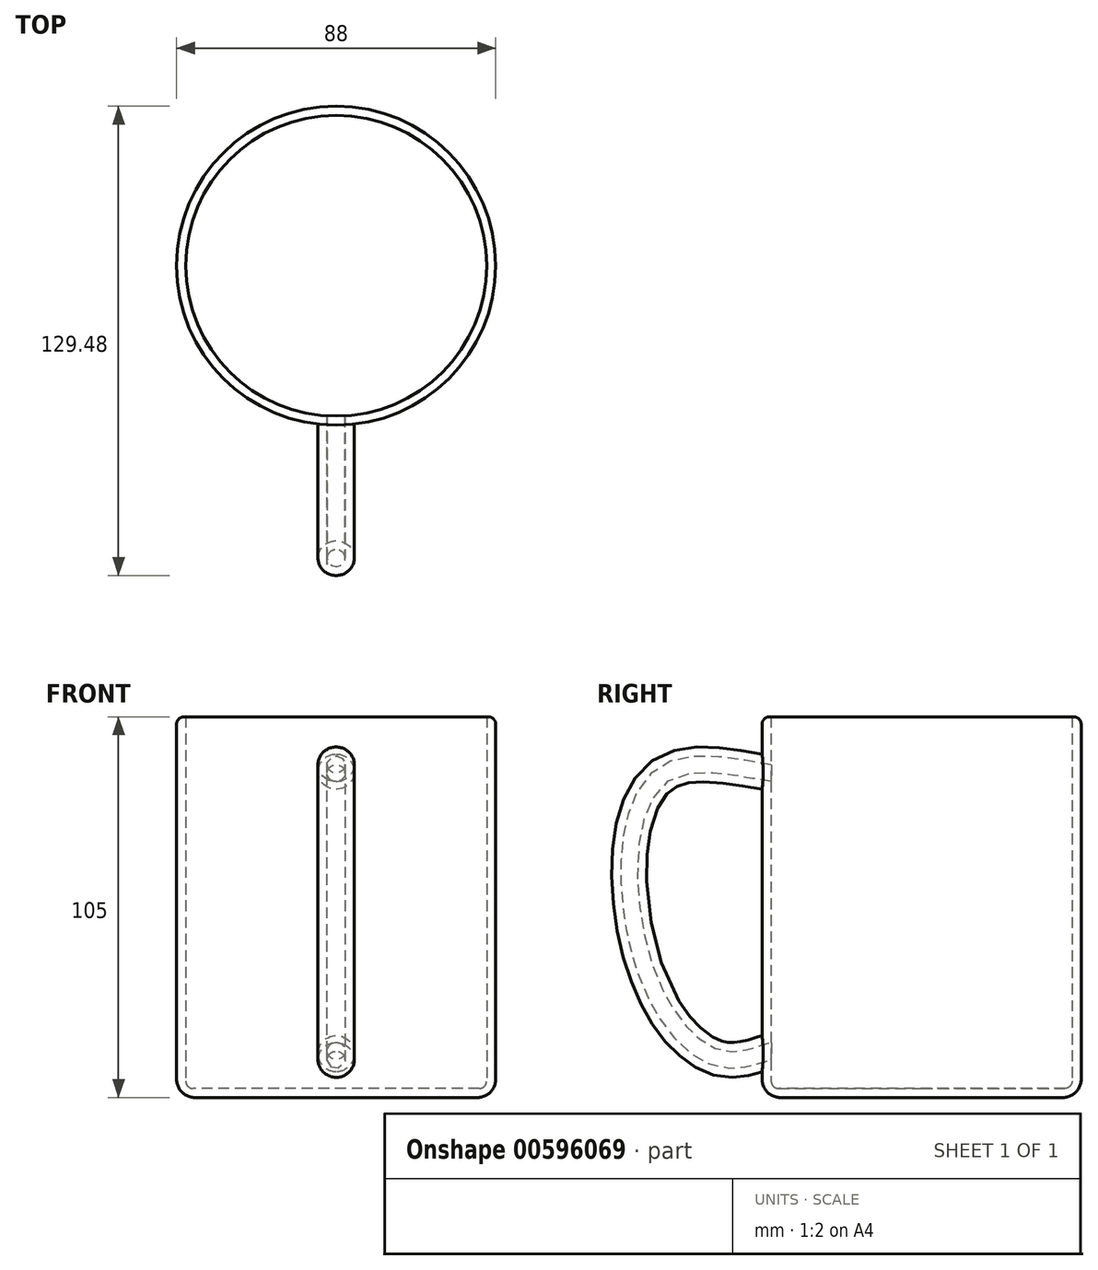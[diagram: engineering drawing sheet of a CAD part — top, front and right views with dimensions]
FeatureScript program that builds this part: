
annotation { "Feature Type Name" : "Feature", "Feature Type Description" : "" }
export const myFeature = defineFeature(function(context is Context, id is Id, definition is map)
    precondition{}
    {
        {
            var Q0;
            Q0=qCreatedBy(makeId("Top.planeOp"),FACE);
            var sketch = newSketch(context, id + "F0", { "sketchPlane" : qUnion([Q0])});
            skCircle(sketch, "E0", {"center": v(0, 0) * mm, "radius": 44 * mm});
            skSolve(sketch);
        }
        {
            var Q0;
            Q0 = qSketchRegion(id + "F0", true);
            extrude(context, id + "F1", {"entities" : qUnion([Q0]), "depth" : 105 * mm, "offsetDistance" : 25 * mm});
        }
        {
            var Q0;
            Q0=qCreatedBy(makeId("Front.planeOp"),FACE);
            cPlane(context, id + "F2", {"entities" : qUnion([Q0]), "cplaneType" : CPlaneType.OFFSET, "offset" : 44 * mm, "width" : 150 * mm, "height" : 150 * mm});
        }
        {
            var Q0;
            Q0=qCreatedBy(makeId("Right.planeOp"),FACE);
            var sketch = newSketch(context, id + "F3", { "sketchPlane" : qUnion([Q0])});
            skFitSpline(sketch, "E1", {"points": [v(-32.55, 87.3) * mm, v(-70.67, 87.84) * mm, v(-75.23, 36.61) * mm, v(-53.82, 11.84) * mm, v(-35.55, 15.04) * mm], "startDerivative": vector(-132.04, -2.06) * mm, "endDerivative": vector(102.56, -2.85) * mm});
            skSolve(sketch);
        }
        {
            var Q0;
            Q0=qCreatedBy(id+"F2.planeOp",FACE);
            var sketch = newSketch(context, id + "F4", { "sketchPlane" : qUnion([Q0])});
            skCircle(sketch, "E2", {"center": v(0, 12.07) * mm, "radius": 5 * mm});
            skSolve(sketch);
        }
        {
            var Q0;
            Q0=makeQuery(id+"F4.imprint","IMPRINT",FACE,{"disambiguationData":[TD([[makeQuery(id+"F4.imprint","IMPRINT",EDGE,{"derivedFrom":sQuery(id+"F4.wireOp",EDGE,"E2")}),1.0]])]});
            var Q1;
            Q1=sQuery(id+"F3.wireOp",EDGE,"E1");
            sweep(context, id + "F5", {"operationType" : NewBodyOperationType.ADD, "profiles" : qUnion([Q0]), "path" : qUnion([Q1])});
        }
        {
            var Q0;
            Q0=makeQuery(id+"F1.opExtrude","CAP_FACE",FACE,{"disambiguationData":[OSD([sQuery(id+"F0.wireOp",EDGE,"E0")])],"isStart":false});
            shell(context, id + "F6", {"entities" : qUnion([Q0]), "thickness" : 2.5 * mm});
        }
        {
            var Q0;
            Q0=makeQuery(id+"F1.opExtrude","CAP_EDGE",EDGE,{"disambiguationData":[OSD([sQuery(id+"F0.wireOp",EDGE,"E0")])],"isStart":false});
            fillet(context, id + "F7", {"entities" : qUnion([Q0]), "radius" : 2 * mm, "tangentPropagation" : true, "allowEdgeOverflow" : false});
        }
        {
            var Q0;
            {var subQ0=sQuery(id+"F0.wireOp",EDGE,"E0");Q0=makeQuery(id+"F6.opShell","OFFSET_FACE",FACE,{"disambiguationData":[OSD([subQ0]),TDD([makeQuery(id+"F1.opExtrude","CAP_FACE",FACE,{"disambiguationData":[OSD([subQ0])],"isStart":true})])]});}
            fillet(context, id + "F8", {"entities" : qUnion([Q0]), "radius" : 2 * mm, "tangentPropagation" : true, "allowEdgeOverflow" : false});
        }
        {
            var Q0;
            Q0=makeQuery(id+"F1.opExtrude","CAP_FACE",FACE,{"disambiguationData":[OSD([sQuery(id+"F0.wireOp",EDGE,"E0")])],"isStart":true});
            fillet(context, id + "F9", {"entities" : qUnion([Q0]), "radius" : 5 * mm, "tangentPropagation" : true, "allowEdgeOverflow" : false});
        }
    });
